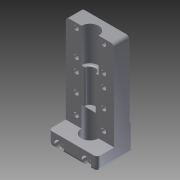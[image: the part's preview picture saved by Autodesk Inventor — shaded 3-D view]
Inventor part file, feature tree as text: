
AUTODESK INVENTOR PART (.ipt)
format: ipt  version: 2012 (Build 160160000, 160)  size: 379,392 bytes
history: native  units: mm
features: extrude x12, sketch x12, fillet x6
ambient origin geometry x8: Origin, YZ Plane, XZ Plane, XY Plane, X Axis, Y Axis, Z Axis, Center Point
bodies: Solid1 (feature_tree)
feature tree (30):
  extrude  "Extrusion1"  Depth=30.0mm
  sketch  "Sketch2"  dims[d2=21.2mm d3=15.0mm]
  sketch  "Sketch3"  dims[d4=9.0mm d5=90.0mm d6=0.0mm]
  extrude  "Extrusion2"  Depth=15.0mm
  extrude  "Extrusion3"  Depth=90.0mm TaperAngle=0.0deg
  extrude  "Extrusion4"  Depth=15.0mm
  extrude  "Extrusion5"  Depth=12.0mm
  extrude  "Extrusion6"  Depth=30.0mm TaperAngle=0.0deg
  extrude  "Extrusion7"  Depth=9.2mm
  fillet  "Fillet1"  Radius=4.0mm
  extrude  "Extrusion8"  Depth=4.0mm
  fillet  "Fillet2"  Radius=22.0mm
  fillet  "Fillet3"  Radius=9.2mm
  fillet  "Fillet4"  Radius=4.0mm
  extrude  "Extrusion9"  Depth=4.0mm
  fillet  "Fillet5"  Radius=16.0mm
  fillet  "Fillet6"  [1 undecoded]
  extrude  "Extrusion11"  Depth=7.0mm TaperAngle=0.0deg
  extrude  "Extrusion12"  Depth=4.0mm TaperAngle=0.0deg
  extrude  "Extrusion10"  Depth=24.0mm
  sketch  "Sketch1"  dims[d0=42.4mm d1=30.0mm]
  sketch  "Sketch4"  dims[d7=15.0mm d8=15.0mm]
  sketch  "Sketch5"  dims[d9=30.0mm d10=0.0mm d11=12.0mm]
  sketch  "Sketch6"  dims[d12=15.0mm d13=0.0mm d14=30.0mm d15=0.0mm]
  sketch  "Sketch7"  dims[d16=4.2mm d18=9.2mm d19=4.0mm]
  sketch  "Sketch8"  dims[d20=22.0mm d21=4.0mm d22=22.0mm d23=9.2mm d24=4.0mm]
  sketch  "Sketch9"  dims[d25=16.0mm d26=4.0mm d27=16.0mm d28=0.0mm d29=0.0mm]
  sketch  "Sketch10"  dims[d30=7.1mm d31=7.0mm d32=0.0mm]
  sketch  "Sketch11"  dims[d33=8.5mm d35=4.0mm d36=0.0mm]
  sketch  "Sketch12"  dims[d37=3.0mm d38=24.0mm d39=1.0mm d40=0.0mm d41=3.0mm d42=3.0mm d43=1.0mm d44=0.2mm d45=0.0mm d46=3.0mm d47=6.0mm d48=29.0mm d49=29.0mm d50=0.2mm d51=0.0mm d52=6.0mm d53=6.0mm d54=1.0mm d55=4.2mm d56=9.2mm d57=37.0mm d58=16.0mm d59=9.2mm d60=10.0mm d61=0.0mm d62=6.0mm d63=0.0mm]
note: 1 required parameter value undecoded (feature->parameter linkage not recoverable at this tier; creation-order binding heuristic only, values carry confidence <= 0.55)
